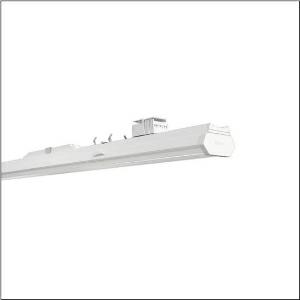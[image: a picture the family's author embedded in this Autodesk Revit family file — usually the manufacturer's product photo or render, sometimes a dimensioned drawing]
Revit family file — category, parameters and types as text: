
# Revit family: licross_r__11_protected_ho_51td1bdn4e5m3s_7495
name_source: partatom
category: Lighting Fixtures
units: mm (PartAtom-declared; Revit-internal decimal feet)

## family parameters
Cut with Voids When Loaded = No
Host = Face
Light Source = No
Part Type = Normal
Room Calculation Point = No
Round Connector Dimension = Use Diameter
Shared = No

## types (1)
- --- (1 x LED, 920 lm, 7.4 W, 4000K)
    Apparent Load = 7 VA
    CIE Flux Codes = 54 82 95 97 100
    Color Rendering = 80
    Color Temperature = 4000K
    Default Elevation = 1800 mm
    Description = Licross® 11 Protected HO, luminaire insert, of sheet steel, galvanised, coil coated, white, length: 1.500mm, width: 90mm, height: 101mm, LED rated luminous flux: 14.500lm, light colour: 840, control gear: DALI 2 (for two DALI lines), with plug, 6-pole, with phase selection, for trunking rail, 14-core, mains connection: 220..240V, AC, 50/60Hz, rated input power: 91W, for trunking rail, 14-core, halogen-free wiring, for emergency light function, converter,control gear: single battery element, battery: LiFePO4, 9Ah, primary optical cover: cover, of PMMA, light emission: direct distribution, primary light characteristic: symmetric, protection rating (complete): IP54, insulation class (complete): insulation class I (protective earthing), certification: CE, UKCA, protection symbol: D if used in an environment with non-conductive dust loads with corresponding accessories, impact resistance: IK06, permissible ambient temperature for indoor applications: +5..+30°C, standard: EN 60598-2-22, LABS conformity tested according to VDMA 24364:2018-05, reducing of maximum allowable ambient temperature of 5°C with ceiling mounting, corresponds to IFS (International Featured Standards) requirements for safety and quality in the food industry, packaging unit: 1 piece
    Height = 92 mm
    Lamp = 1 x LED
    Lamp Light Flux = 920 lm
    Lamp Power = 7.4 W
    Lamp count = 1
    Length = 1500 mm
    Luminous efficacy = 124 lm/W
    Manufacturer = Siteco
    ModVariant = No
    Model = 51TD1BDN4E5M3S
    Mounting Place = Ceiling
    Mounting Type = Pendant
    Number of Poles = 1
    OnlyDefault = Yes
    Power Factor = 1
    Product Name = Licross® 11 Protected HO
    Product group = luminaire insert
    ProductGroupID = 902
    Protection Class = Protection class I
    Protection Degree = IP 54
    RLX_Detail_Level = 1
    RLX_Emergency_Light_Flux = 0 lm
    RLX_Emergency_Type = 0
    RLX_Emergency_Type_DB = No
    RlxData = <blob elided: 24809 chars, md5=d979d714>
    Socket = socket
    Standby Power = 0 W
    System Light Flux = 920 lm
    System Power = 7 W
    Type Comments = : emergency light operation: 3 h
    Type Image = l_1256145.jpg
    URL = http://relux.com
    VarID = @adj_091256
    Voltage = 0 V
    Weight = 0.00 kg
    Width = 88 mm

## geometry (parser evidence)
native form markers: Blend x4, Sweep x12
no freeform markers — native parametric forms only
